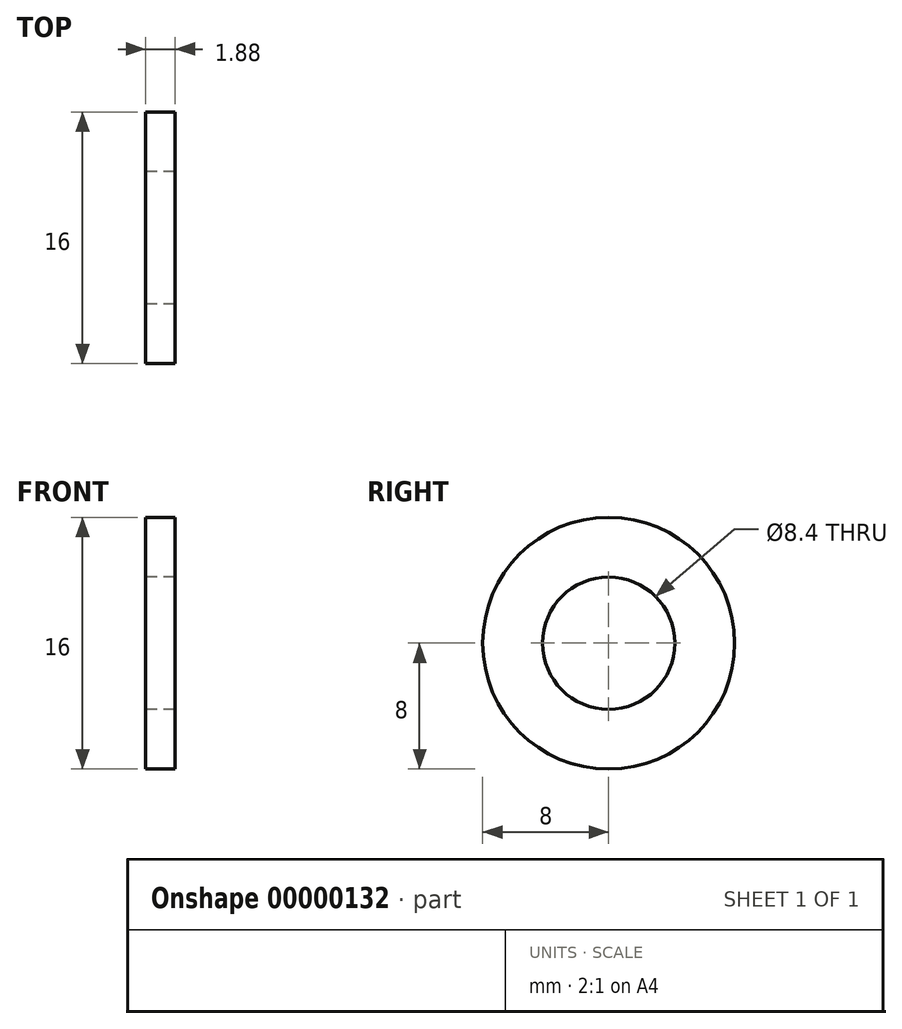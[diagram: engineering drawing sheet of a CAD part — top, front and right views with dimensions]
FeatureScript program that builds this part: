
annotation { "Feature Type Name" : "Feature", "Feature Type Description" : "" }
export const myFeature = defineFeature(function(context is Context, id is Id, definition is map)
    precondition{}
    {
        {
            var Q0;
            Q0 = qCreatedBy(makeId("Right.planeOp"), FACE);
            var sketch = newSketch(context, id + "F0", { "sketchPlane" : qUnion([Q0])});
            skCircle(sketch, "E0", {"center": v(0, 0) * mm, "radius": 8 * mm});
            skCircle(sketch, "E1", {"center": v(0, 0) * mm, "radius": 4.2 * mm});
            skSolve(sketch);
        }
        {
            var Q0;
            Q0=makeQuery(id+"F0.imprint","IMPRINT",FACE,{"disambiguationData":[TD([[makeQuery(id+"F0.imprint","IMPRINT",EDGE,{"derivedFrom":sQuery(id+"F0.wireOp",EDGE,"E0")}),1.0]])]});
            extrude(context, id + "F1", {"entities" : qUnion([Q0]), "depth" : 1.88 * mm});
        }
    });
